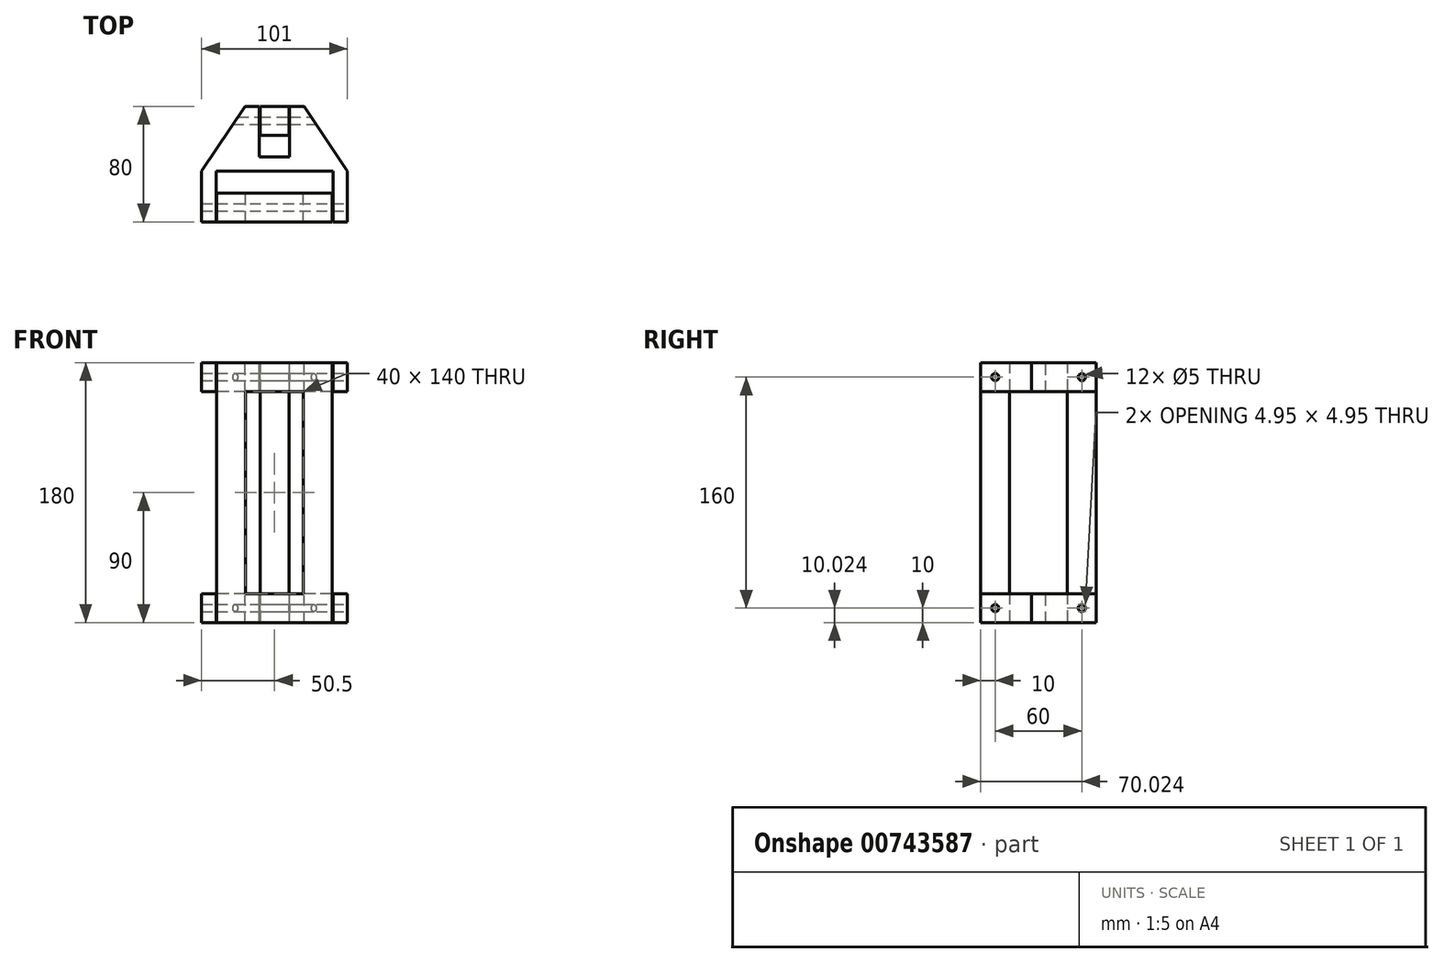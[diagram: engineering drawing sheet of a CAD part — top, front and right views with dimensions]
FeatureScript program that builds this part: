
annotation { "Feature Type Name" : "Feature", "Feature Type Description" : "" }
export const myFeature = defineFeature(function(context is Context, id is Id, definition is map)
    precondition{}
    {
        {
            assignVariable(context, id + "F0", {"name" : "HingTollerance", "anyValue" : 0.5});
        }
        {
            assignVariable(context, id + "F1", {"name" : "LegThighLength", "anyValue" : 180});
        }
        {
            assignVariable(context, id + "F2", {"name" : "LegSparThickness", "anyValue" : 20});
        }
        {
            var Q0;
            Q0=qCreatedBy(makeId("Front.planeOp"),FACE);
            var sketch = newSketch(context, id + "F3", { "sketchPlane" : qUnion([Q0])});
            skLineSegment(sketch, "E0.bottom", {"start": v(-100, 0) * mm, "end": v(-20, 0) * mm});
            skLineSegment(sketch, "E0.top", {"start": v(-100, -180) * mm, "end": v(-20, -180) * mm});
            skLineSegment(sketch, "E0.left", {"start": v(-100, 0) * mm, "end": v(-100, -180) * mm});
            skLineSegment(sketch, "E0.right", {"start": v(-20, 0) * mm, "end": v(-20, -180) * mm});
            skLineSegment(sketch, "E1.bottom", {"start": v(-80, -20) * mm, "end": v(-40, -20) * mm});
            skLineSegment(sketch, "E1.top", {"start": v(-80, -160) * mm, "end": v(-40, -160) * mm});
            skLineSegment(sketch, "E1.left", {"start": v(-80, -20) * mm, "end": v(-80, -160) * mm});
            skLineSegment(sketch, "E1.right", {"start": v(-40, -20) * mm, "end": v(-40, -160) * mm});
            skSolve(sketch);
        }
        {
            var Q0;
            Q0=makeQuery(id+"F3.imprint","IMPRINT",FACE,{"disambiguationData":[TD([[makeQuery(id+"F3.imprint","IMPRINT",EDGE,{"derivedFrom":sQuery(id+"F3.wireOp",EDGE,"E0.bottom")}),-1.0]])]});
            extrude(context, id + "F4", {"entities" : qUnion([Q0]), "depth" : (getVariable(context, 'LegSparThickness')) * mm, "offsetDistance" : 25 * mm});
        }
        {
            var Q0;
            Q0=makeQuery(id+"F4.opExtrude","SWEPT_FACE",FACE,{"disambiguationData":[OSD([sQuery(id+"F3.wireOp",EDGE,"E0.bottom")])]});
            cPlane(context, id + "F5", {"entities" : qUnion([Q0]), "cplaneType" : CPlaneType.OFFSET, "offset" : 0 * mm, "width" : 150 * mm, "height" : 150 * mm});
        }
        {
            var Q0;
            Q0=qCreatedBy(id+"F5.planeOp",FACE);
            var sketch = newSketch(context, id + "F6", { "sketchPlane" : qUnion([Q0])});
            skLineSegment(sketch, "E2.bottom", {"start": v(-100.5, -20) * mm, "end": v(-110.5, -20) * mm});
            skLineSegment(sketch, "E2.left", {"start": v(-100.5, -20) * mm, "end": v(-100.5, 15) * mm});
            skLineSegment(sketch, "E2.right", {"start": v(-110.5, -20) * mm, "end": v(-110.5, 15) * mm});
            skLineSegment(sketch, "E3.bottom", {"start": v(-19.5, -20) * mm, "end": v(-9.5, -20) * mm});
            skLineSegment(sketch, "E3.left", {"start": v(-19.5, -20) * mm, "end": v(-19.5, 15) * mm});
            skLineSegment(sketch, "E3.right", {"start": v(-9.5, -20) * mm, "end": v(-9.5, 15) * mm});
            skLineSegment(sketch, "E4.bottom", {"start": v(-70.5, 60) * mm, "end": v(-80.5, 60) * mm});
            skLineSegment(sketch, "E4.left", {"start": v(-70.5, 60) * mm, "end": v(-70.5, 25) * mm});
            skLineSegment(sketch, "E5.bottom", {"start": v(-49.5, 60) * mm, "end": v(-39.5, 60) * mm});
            skLineSegment(sketch, "E5.left", {"start": v(-49.5, 60) * mm, "end": v(-49.5, 25) * mm});
            skLineSegment(sketch, "E6.bottom", {"start": v(-70.5, 25) * mm, "end": v(-49.5, 25) * mm});
            skLineSegment(sketch, "E7", {"start": v(-9.5, 15) * mm, "end": v(-39.5, 60) * mm});
            skLineSegment(sketch, "E8", {"start": v(-80.5, 60) * mm, "end": v(-110.5, 15) * mm});
            skLineSegment(sketch, "E9", {"start": v(-19.5, 15) * mm, "end": v(-100.5, 15) * mm});
            skSolve(sketch);
        }
        {
            var Q0;
            Q0=makeQuery(id+"F6.imprint","IMPRINT",FACE,{"disambiguationData":[TD([[makeQuery(id+"F6.imprint","IMPRINT",EDGE,{"derivedFrom":sQuery(id+"F6.wireOp",EDGE,"E2.bottom")}),-1.0]])]});
            extrude(context, id + "F7", {"entities" : qUnion([Q0]), "oppositeDirection" : true, "depth" : (getVariable(context, 'LegSparThickness')) * mm, "offsetDistance" : 25 * mm});
        }
        {
            var Q0;
            Q0=makeQuery(id+"F6.imprint","IMPRINT",FACE,{"disambiguationData":[TD([[makeQuery(id+"F6.imprint","IMPRINT",EDGE,{"derivedFrom":sQuery(id+"F6.wireOp",EDGE,"E2.bottom")}),-1.0]])]});
            extrude(context, id + "F8", {"entities" : qUnion([Q0]), "oppositeDirection" : true, "depth" : (getVariable(context, 'LegThighLength')) * mm, "offsetDistance" : 25 * mm, "hasSecondDirection" : true, "secondDirectionOppositeDirection" : true, "secondDirectionDepth" : (getVariable(context, 'LegThighLength') - getVariable(context, 'LegSparThickness')) * mm});
        }
        {
            var Q0;
            Q0=qCreatedBy(makeId("Right.planeOp"),FACE);
            var sketch = newSketch(context, id + "F9", { "sketchPlane" : qUnion([Q0])});
            skCircle(sketch, "E10", {"center": v(-10, -10) * mm, "radius": 2.5 * mm});
            skLineSegment(sketch, "E11", {"start": v(-10, -10) * mm, "end": v(-10, -196.18) * mm, "construction": true});
            skCircle(sketch, "E12", {"center": v(-10, -170) * mm, "radius": 2.5 * mm});
            skLineSegment(sketch, "E13", {"start": v(-48.85, -10) * mm, "end": v(95.89, -10) * mm, "construction": true});
            skLineSegment(sketch, "E14", {"start": v(-48.04, -170) * mm, "end": v(95.89, -170) * mm, "construction": true});
            skLineSegment(sketch, "E15", {"start": v(50, 11.27) * mm, "end": v(50, -196.18) * mm, "construction": true});
            skCircle(sketch, "E16", {"center": v(50, -10) * mm, "radius": 2.5 * mm});
            skCircle(sketch, "E17", {"center": v(50, -170) * mm, "radius": 2.5 * mm});
            skLineSegment(sketch, "E18", {"start": v(50, -170) * mm, "end": v(-30, -90) * mm, "construction": true});
            skLineSegment(sketch, "E19", {"start": v(-30, -90) * mm, "end": v(50, -10) * mm, "construction": true});
            skArc(sketch, "E20", {"start": v(-9.95, -7.5) * mm, "mid": v(6.7, -51.53) * mm, "end": v(50, -70) * mm, "construction": true});
            skArc(sketch, "E21", {"start": v(50, -110) * mm, "mid": v(6.7, -128.47) * mm, "end": v(-9.95, -172.5) * mm, "construction": true});
            skPoint(sketch, "E22", {"position": v(7.57, -52.43) * mm});
            skPoint(sketch, "E23", {"position": v(7.57, -127.57) * mm});
            skLineSegment(sketch, "E24", {"start": v(7.57, 9.4) * mm, "end": v(7.57, -196.18) * mm, "construction": true});
            skLineSegment(sketch, "E25", {"start": v(50, -196.18) * mm, "end": v(-10, -196.18) * mm, "construction": true});
            skSolve(sketch);
        }
        {
            var Q0;
            Q0=makeQuery(id+"F7.opExtrude","SWEPT_FACE",FACE,{"disambiguationData":[OSD([sQuery(id+"F6.wireOp",EDGE,"E4.left")])]});
            cPlane(context, id + "F10", {"entities" : qUnion([Q0]), "cplaneType" : CPlaneType.OFFSET, "offset" : (getVariable(context, 'HingTollerance')) * mm, "width" : 150 * mm, "height" : 150 * mm});
        }
        {
            var Q0;
            Q0=qCreatedBy(id+"F10.planeOp",FACE);
            var sketch = newSketch(context, id + "F11", { "sketchPlane" : qUnion([Q0])});
            skLineSegment(sketch, "E26.bottom", {"start": v(40, 0) * mm, "end": v(60, 0) * mm});
            skLineSegment(sketch, "E26.top", {"start": v(40, -180) * mm, "end": v(60, -180) * mm});
            skLineSegment(sketch, "E26.left", {"start": v(40, 0) * mm, "end": v(40, -180) * mm});
            skLineSegment(sketch, "E26.right", {"start": v(60, 0) * mm, "end": v(60, -180) * mm});
            skLineSegment(sketch, "E27", {"start": v(50, 21.07) * mm, "end": v(50, -199.24) * mm, "construction": true});
            skPoint(sketch, "E27.startSnap0", {"position": v(50, 0) * mm});
            skLineSegment(sketch, "E28", {"start": v(-10, 21.07) * mm, "end": v(-10, -199.24) * mm, "construction": true});
            skSolve(sketch);
        }
        {
            var Q0;
            Q0=makeQuery(id+"F11.imprint","IMPRINT",FACE,{"disambiguationData":[TD([[makeQuery(id+"F11.imprint","IMPRINT",EDGE,{"derivedFrom":sQuery(id+"F11.wireOp",EDGE,"E26.bottom")}),-1.0]])]});
            extrude(context, id + "F12", {"entities" : qUnion([Q0]), "depth" : (getVariable(context, 'LegSparThickness')) * mm, "offsetDistance" : 25 * mm});
        }
        {
            var Q0;
            Q0=makeQuery(id+"F9.imprint","IMPRINT",FACE,{"disambiguationData":[TD([[makeQuery(id+"F9.imprint","IMPRINT",EDGE,{"derivedFrom":sQuery(id+"F9.wireOp",EDGE,"E10")}),1.0]])]});
            var Q1;
            Q1=makeQuery(id+"F9.imprint","IMPRINT",FACE,{"disambiguationData":[TD([[makeQuery(id+"F9.imprint","IMPRINT",EDGE,{"derivedFrom":sQuery(id+"F9.wireOp",EDGE,"E12")}),1.0]])]});
            var Q2;
            Q2=makeQuery(id+"F9.imprint","IMPRINT",FACE,{"disambiguationData":[TD([[makeQuery(id+"F9.imprint","IMPRINT",EDGE,{"derivedFrom":sQuery(id+"F9.wireOp",EDGE,"E16")}),1.0]])]});
            var Q3;
            Q3=makeQuery(id+"F9.imprint","IMPRINT",FACE,{"disambiguationData":[TD([[makeQuery(id+"F9.imprint","IMPRINT",EDGE,{"derivedFrom":sQuery(id+"F9.wireOp",EDGE,"E17")}),1.0]])]});
            extrude(context, id + "F13", {"entities" : qUnion([Q0, Q1, Q2, Q3]), "operationType" : NewBodyOperationType.REMOVE, "endBound" : BoundingType.THROUGH_ALL, "oppositeDirection" : true, "depth" : 25 * mm, "offsetDistance" : 25 * mm});
        }
    });
